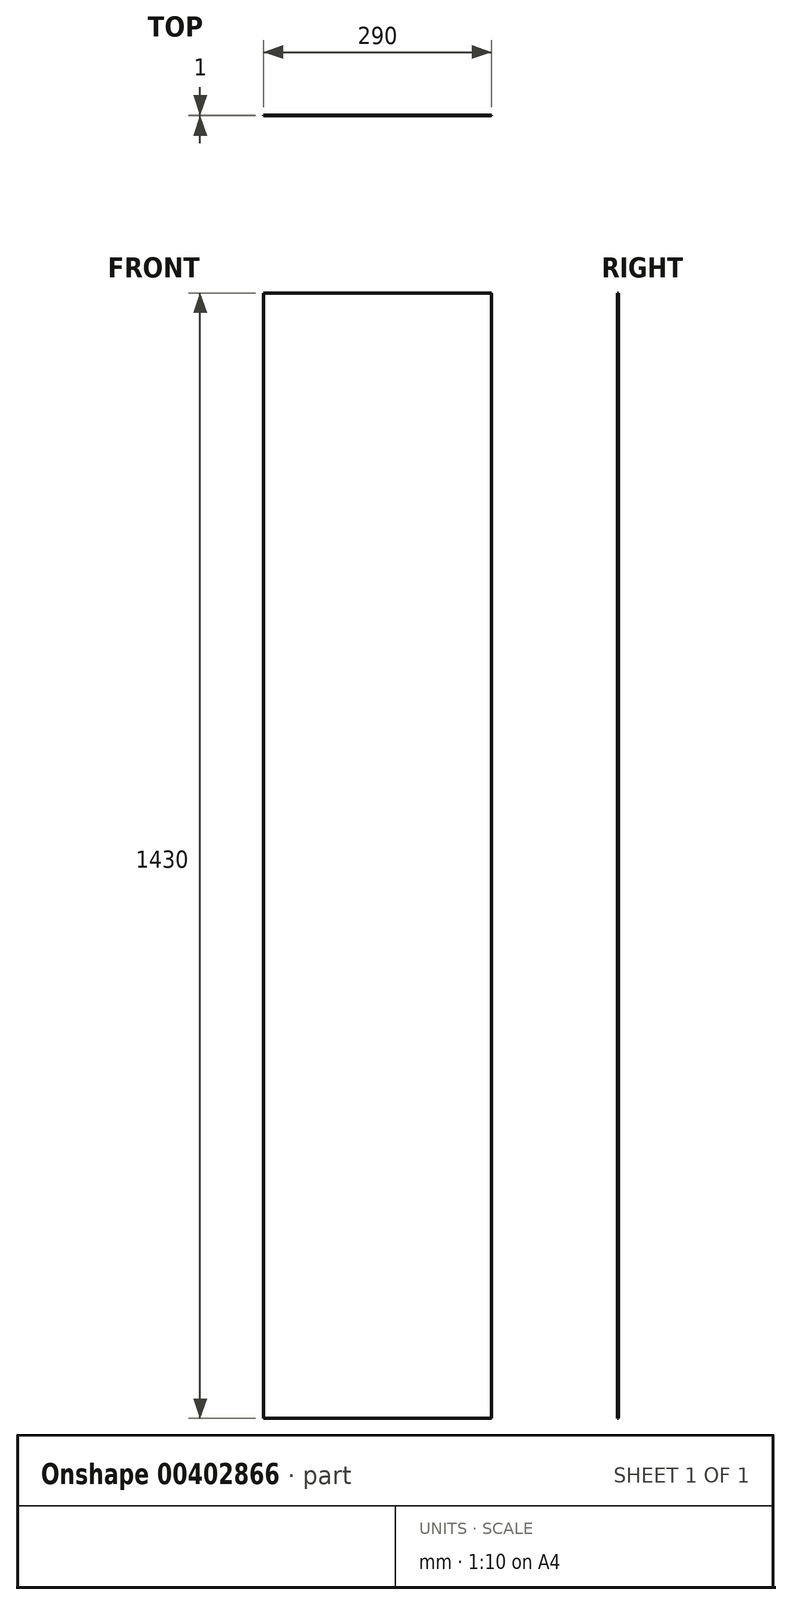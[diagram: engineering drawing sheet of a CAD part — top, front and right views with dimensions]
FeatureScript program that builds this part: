
annotation { "Feature Type Name" : "Feature", "Feature Type Description" : "" }
export const myFeature = defineFeature(function(context is Context, id is Id, definition is map)
    precondition{}
    {
        {
            var Q0;
            Q0=qCreatedBy(makeId("Front.planeOp"),FACE);
            var sketch = newSketch(context, id + "F0", { "sketchPlane" : qUnion([Q0])});
            skLineSegment(sketch, "E0.bottom", {"start": v(-145, 715) * mm, "end": v(145, 715) * mm});
            skLineSegment(sketch, "E0.top", {"start": v(-145, -715) * mm, "end": v(145, -715) * mm});
            skLineSegment(sketch, "E0.left", {"start": v(-145, 715) * mm, "end": v(-145, -715) * mm});
            skLineSegment(sketch, "E0.right", {"start": v(145, 715) * mm, "end": v(145, -715) * mm});
            skPoint(sketch, "E0.middle", {"position": v(0, 0) * mm});
            skSolve(sketch);
        }
        {
            var Q0;
            Q0=makeQuery(id+"F0.imprint","IMPRINT",FACE,{"disambiguationData":[TD([[makeQuery(id+"F0.imprint","IMPRINT",EDGE,{"derivedFrom":sQuery(id+"F0.wireOp",EDGE,"E0.bottom")}),-1.0]])]});
            extrude(context, id + "F1", {"entities" : qUnion([Q0]), "depth" : 1 * mm});
        }
    });
